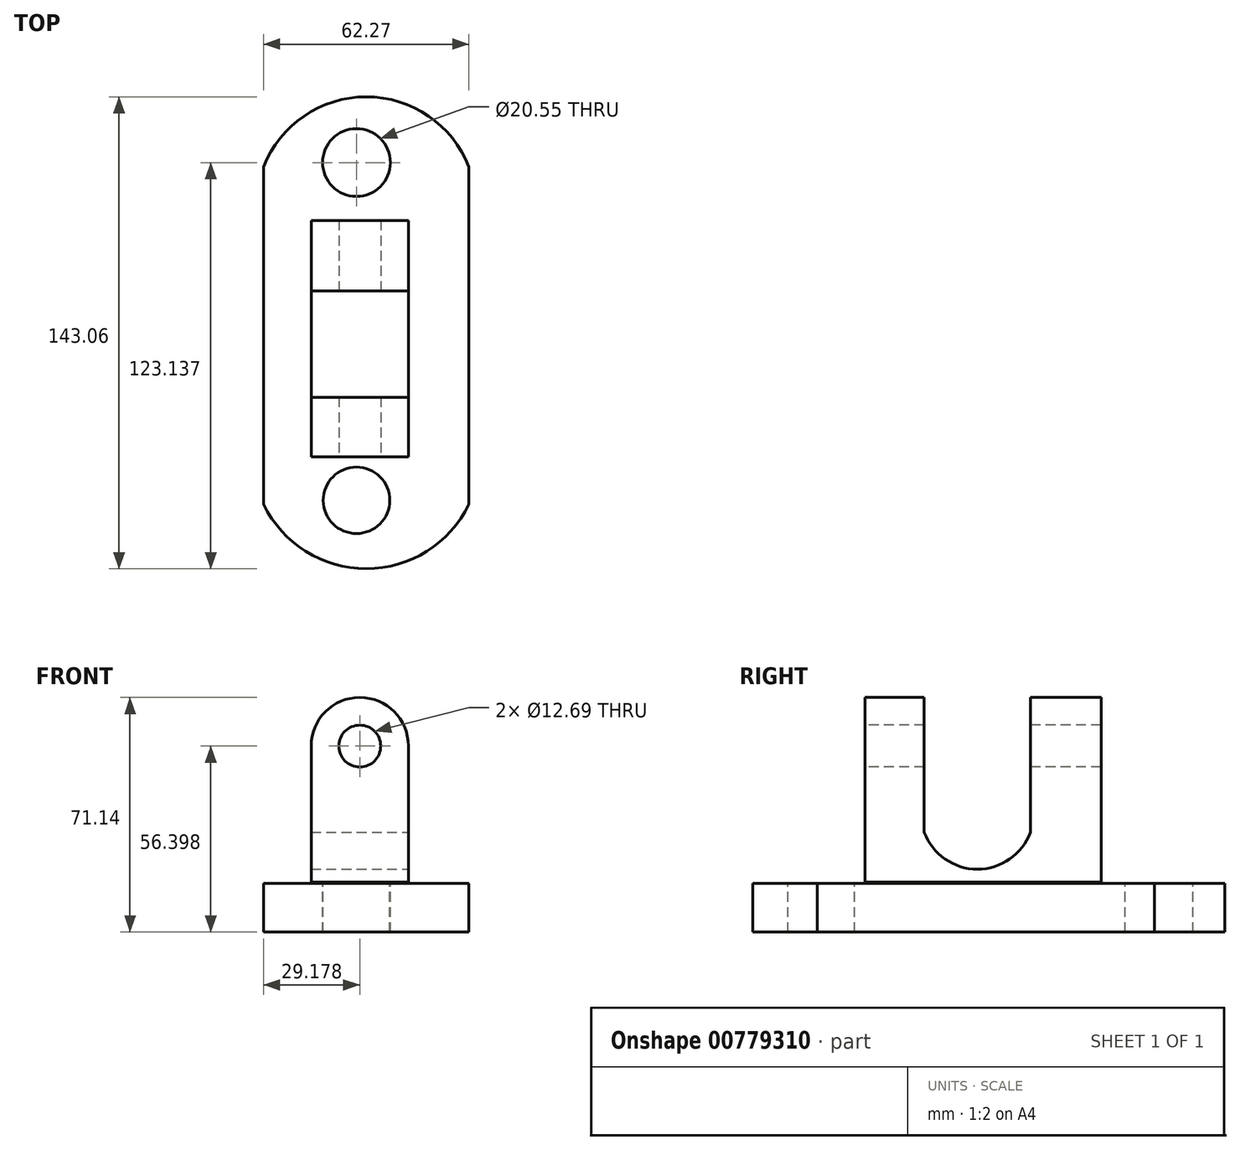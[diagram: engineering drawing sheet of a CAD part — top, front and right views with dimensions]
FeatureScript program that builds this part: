
annotation { "Feature Type Name" : "Feature", "Feature Type Description" : "" }
export const myFeature = defineFeature(function(context is Context, id is Id, definition is map)
    precondition{}
    {
        {
            var Q0;
            Q0=qCreatedBy(makeId("Top.planeOp"),FACE);
            var sketch = newSketch(context, id + "F0", { "sketchPlane" : qUnion([Q0])});
            skLineSegment(sketch, "E0.left", {"start": v(-37.45, 56.1) * mm, "end": v(-37.45, -46.17) * mm});
            skLineSegment(sketch, "E0.right", {"start": v(24.82, 56.1) * mm, "end": v(24.82, -46.17) * mm});
            skArc(sketch, "E1", {"start": v(24.82, 56.1) * mm, "mid": v(-6.32, 77.35) * mm, "end": v(-37.45, 56.1) * mm});
            skArc(sketch, "E2", {"start": v(-37.45, -46.17) * mm, "mid": v(-6.32, -65.7) * mm, "end": v(24.82, -46.17) * mm});
            skSolve(sketch);
        }
        {
            var Q0;
            Q0=makeQuery(id+"F0.imprint","IMPRINT",FACE,{"disambiguationData":[TD([[makeQuery(id+"F0.imprint","IMPRINT",EDGE,{"derivedFrom":sQuery(id+"F0.wireOp",EDGE,"E0.left")}),1.0]])]});
            extrude(context, id + "F1", {"entities" : qUnion([Q0]), "depth" : 14.73 * mm, "offsetDistance" : 25.4 * mm});
        }
        {
            var Q0;
            Q0=qCreatedBy(makeId("Front.planeOp"),FACE);
            var sketch = newSketch(context, id + "F2", { "sketchPlane" : qUnion([Q0])});
            skLineSegment(sketch, "E3.top", {"start": v(-23.01, 15.19) * mm, "end": v(6.47, 15.19) * mm});
            skLineSegment(sketch, "E3.left", {"start": v(-23.01, 56.4) * mm, "end": v(-23.01, 15.19) * mm});
            skLineSegment(sketch, "E3.right", {"start": v(6.47, 56.4) * mm, "end": v(6.47, 15.19) * mm});
            skArc(sketch, "E4", {"start": v(6.47, 56.4) * mm, "mid": v(-8.27, 71.14) * mm, "end": v(-23.01, 56.4) * mm});
            skCircle(sketch, "E5", {"center": v(-8.27, 56.4) * mm, "radius": 6.35 * mm});
            skSolve(sketch);
        }
        {
            var Q0;
            Q0=makeQuery(id+"F2.imprint","IMPRINT",FACE,{"disambiguationData":[TD([[makeQuery(id+"F2.imprint","IMPRINT",EDGE,{"derivedFrom":sQuery(id+"F2.wireOp",EDGE,"E3.top")}),1.0]])]});
            extrude(context, id + "F3", {"entities" : qUnion([Q0]), "oppositeDirection" : true, "depth" : 39.88 * mm, "offsetDistance" : 25.4 * mm});
        }
        {
            var Q0;
            Q0=makeQuery(id+"F3.opExtrude","CAP_FACE",FACE,{"disambiguationData":[OSD([sQuery(id+"F2.wireOp",EDGE,"E3.top"),sQuery(id+"F2.wireOp",EDGE,"E3.left"),sQuery(id+"F2.wireOp",EDGE,"E3.right"),sQuery(id+"F2.wireOp",EDGE,"E4"),sQuery(id+"F2.wireOp",EDGE,"E5")])],"isStart":true});
            extrude(context, id + "F4", {"entities" : qUnion([Q0]), "operationType" : NewBodyOperationType.ADD, "depth" : 31.75 * mm, "offsetDistance" : 25.4 * mm});
        }
        {
            var Q0;
            Q0=makeQuery(id+"F1.opExtrude","CAP_FACE",FACE,{"disambiguationData":[OSD([sQuery(id+"F0.wireOp",EDGE,"E0.left"),sQuery(id+"F0.wireOp",EDGE,"E0.right"),sQuery(id+"F0.wireOp",EDGE,"E1"),sQuery(id+"F0.wireOp",EDGE,"E2")])],"isStart":false});
            var sketch = newSketch(context, id + "F5", { "sketchPlane" : qUnion([Q0])});
            skCircle(sketch, "E6", {"center": v(-9.29, 57.43) * mm, "radius": 10.27 * mm});
            skCircle(sketch, "E7", {"center": v(-9.29, -44.95) * mm, "radius": 10.08 * mm});
            skSolve(sketch);
        }
        {
            var Q0;
            Q0=makeQuery(id+"F5.imprint","IMPRINT",FACE,{"disambiguationData":[TD([[makeQuery(id+"F5.imprint","IMPRINT",EDGE,{"derivedFrom":sQuery(id+"F5.wireOp",EDGE,"E7")}),1.0]])]});
            extrude(context, id + "F6", {"entities" : qUnion([Q0]), "operationType" : NewBodyOperationType.REMOVE, "endBound" : BoundingType.THROUGH_ALL, "oppositeDirection" : true, "depth" : 25.4 * mm, "offsetDistance" : 25.4 * mm});
        }
        {
            var Q0;
            Q0=makeQuery(id+"F5.imprint","IMPRINT",FACE,{"disambiguationData":[TD([[makeQuery(id+"F5.imprint","IMPRINT",EDGE,{"derivedFrom":sQuery(id+"F5.wireOp",EDGE,"E6")}),1.0]])]});
            extrude(context, id + "F7", {"entities" : qUnion([Q0]), "operationType" : NewBodyOperationType.REMOVE, "endBound" : BoundingType.THROUGH_ALL, "oppositeDirection" : true, "depth" : 25.4 * mm, "offsetDistance" : 25.4 * mm});
        }
        {
            var Q0;
            Q0=qCreatedBy(makeId("Right.planeOp"),FACE);
            var sketch = newSketch(context, id + "F8", { "sketchPlane" : qUnion([Q0])});
            skLineSegment(sketch, "E8.bottom", {"start": v(-13.71, 72.34) * mm, "end": v(18.47, 72.34) * mm});
            skLineSegment(sketch, "E8.left", {"start": v(-13.71, 72.34) * mm, "end": v(-13.71, 30.23) * mm});
            skLineSegment(sketch, "E8.right", {"start": v(18.47, 72.34) * mm, "end": v(18.47, 30.23) * mm});
            skArc(sketch, "E9", {"start": v(-13.71, 30.23) * mm, "mid": v(2.38, 19.08) * mm, "end": v(18.47, 30.23) * mm});
            skSolve(sketch);
        }
        {
            var Q0;
            Q0=makeQuery(id+"F8.imprint","IMPRINT",FACE,{"disambiguationData":[TD([[makeQuery(id+"F8.imprint","IMPRINT",EDGE,{"derivedFrom":sQuery(id+"F8.wireOp",EDGE,"E8.bottom")}),-1.0]])]});
            extrude(context, id + "F9", {"entities" : qUnion([Q0]), "operationType" : NewBodyOperationType.REMOVE, "endBound" : BoundingType.THROUGH_ALL, "oppositeDirection" : true, "depth" : 25.4 * mm, "offsetDistance" : 25.4 * mm});
        }
        {
            var Q0;
            Q0=makeQuery(id+"F8.imprint","IMPRINT",FACE,{"disambiguationData":[TD([[makeQuery(id+"F8.imprint","IMPRINT",EDGE,{"derivedFrom":sQuery(id+"F8.wireOp",EDGE,"E8.bottom")}),-1.0]])]});
            extrude(context, id + "F10", {"entities" : qUnion([Q0]), "operationType" : NewBodyOperationType.REMOVE, "depth" : 47.24 * mm, "offsetDistance" : 25.4 * mm});
        }
    });
